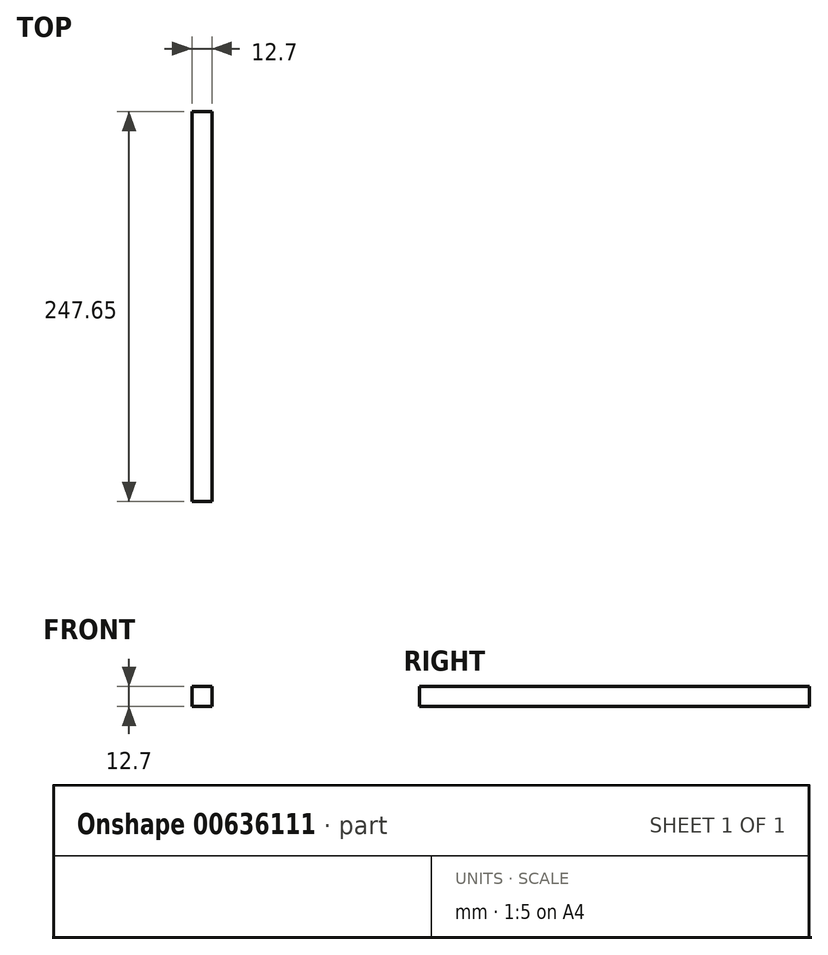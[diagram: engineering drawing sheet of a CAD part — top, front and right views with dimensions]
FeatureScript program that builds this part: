
annotation { "Feature Type Name" : "Feature", "Feature Type Description" : "" }
export const myFeature = defineFeature(function(context is Context, id is Id, definition is map)
    precondition{}
    {
        {
            var Q0;
            Q0=qCreatedBy(makeId("Top.planeOp"),FACE);
            var sketch = newSketch(context, id + "F0", { "sketchPlane" : qUnion([Q0])});
            skLineSegment(sketch, "E0.bottom", {"start": v(-9.53, 234.23) * mm, "end": v(3.17, 234.23) * mm});
            skLineSegment(sketch, "E0.top", {"start": v(-9.53, -13.42) * mm, "end": v(3.17, -13.42) * mm});
            skLineSegment(sketch, "E0.left", {"start": v(-9.53, 234.23) * mm, "end": v(-9.53, -13.42) * mm});
            skLineSegment(sketch, "E0.right", {"start": v(3.17, 234.23) * mm, "end": v(3.17, -13.42) * mm});
            skSolve(sketch);
        }
        {
            var Q0;
            Q0=makeQuery(id+"F0.imprint","IMPRINT",FACE,{"disambiguationData":[TD([[makeQuery(id+"F0.imprint","IMPRINT",EDGE,{"derivedFrom":sQuery(id+"F0.wireOp",EDGE,"E0.bottom")}),-1.0]])]});
            extrude(context, id + "F1", {"entities" : qUnion([Q0]), "depth" : 12.7 * mm, "offsetDistance" : 25.4 * mm});
        }
    });
